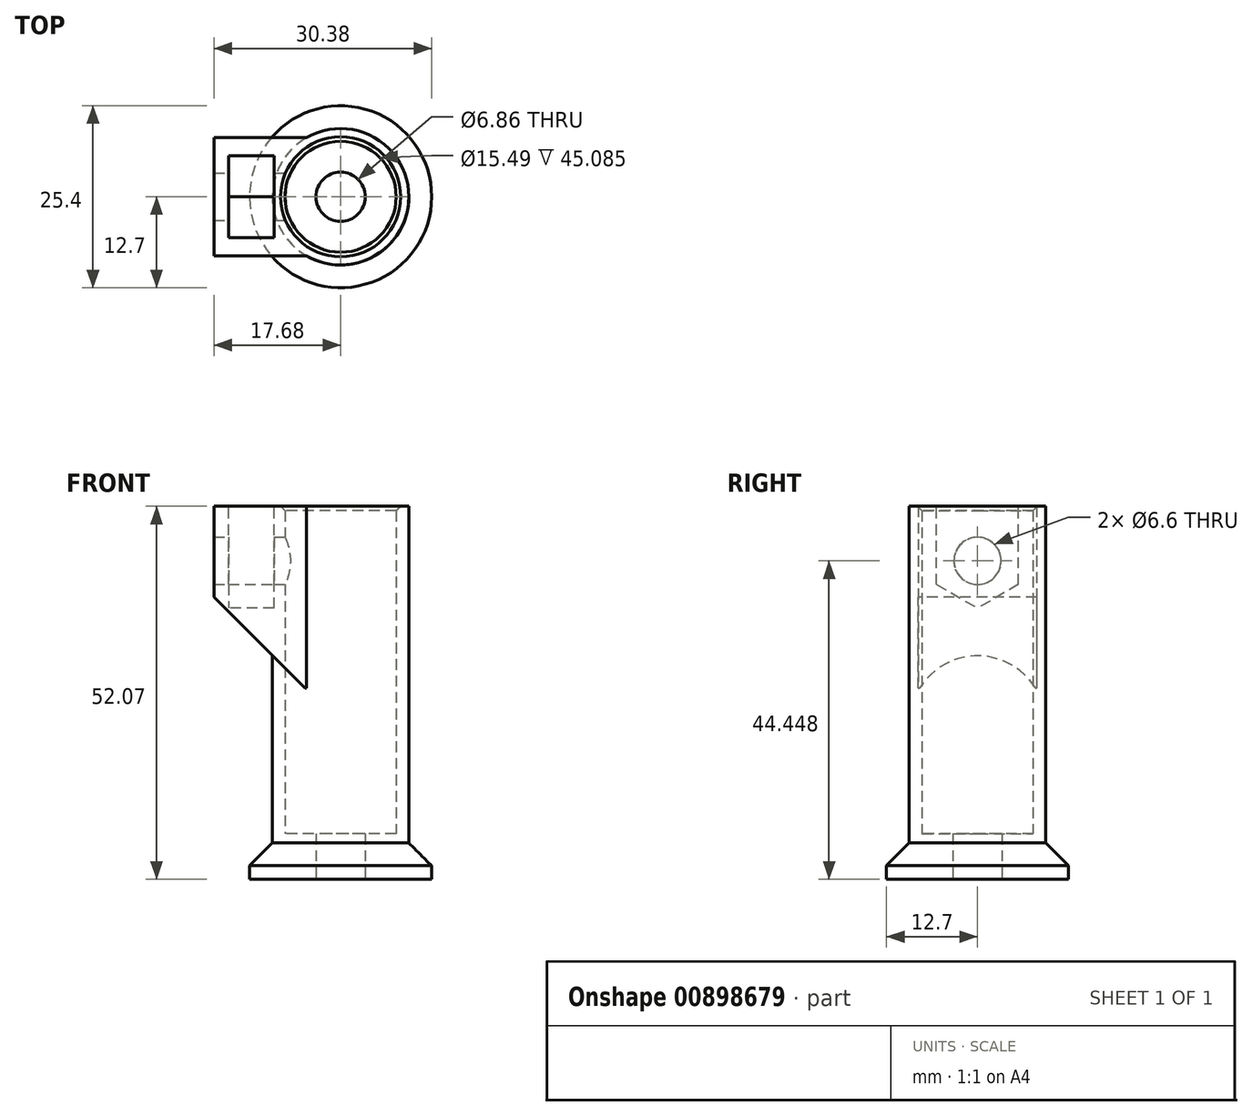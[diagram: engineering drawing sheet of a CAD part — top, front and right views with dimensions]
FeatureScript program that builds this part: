
annotation { "Feature Type Name" : "Feature", "Feature Type Description" : "" }
export const myFeature = defineFeature(function(context is Context, id is Id, definition is map)
    precondition{}
    {
        {
            var Q0;
            Q0=qCreatedBy(makeId("Top.planeOp"),FACE);
            var sketch = newSketch(context, id + "F0", { "sketchPlane" : qUnion([Q0])});
            skCircle(sketch, "E0", {"center": v(0, 0) * mm, "radius": 3.43 * mm});
            skCircle(sketch, "E1", {"center": v(0, 0) * mm, "radius": 12.7 * mm});
            skSolve(sketch);
        }
        {
            var Q0;
            Q0=makeQuery(id+"F0.imprint","IMPRINT",FACE,{"disambiguationData":[TD([[makeQuery(id+"F0.imprint","IMPRINT",EDGE,{"derivedFrom":sQuery(id+"F0.wireOp",EDGE,"E0")}),-1.0]])]});
            extrude(context, id + "F1", {"entities" : qUnion([Q0]), "depth" : 5.08 * mm, "offsetDistance" : 25.4 * mm});
        }
        {
            var Q0;
            Q0=makeQuery(id+"F1.opExtrude","CAP_EDGE",EDGE,{"disambiguationData":[OSD([sQuery(id+"F0.wireOp",EDGE,"E1")])],"isStart":false});
            chamfer(context, id + "F2", {"entities" : qUnion([Q0]), "width" : 3.17 * mm, "tangentPropagation" : true});
        }
        {
            var Q0;
            Q0=makeQuery(id+"F1.opExtrude","CAP_FACE",FACE,{"disambiguationData":[OSD([sQuery(id+"F0.wireOp",EDGE,"E0"),sQuery(id+"F0.wireOp",EDGE,"E1")])],"isStart":false});
            extrude(context, id + "F3", {"entities" : qUnion([Q0]), "operationType" : NewBodyOperationType.ADD, "depth" : 1.27 * mm, "offsetDistance" : 25.4 * mm});
        }
        {
            var Q0;
            Q0=makeQuery(id+"F3.opExtrude","CAP_FACE",FACE,{"disambiguationData":[OSD([sQuery(id+"F0.wireOp",EDGE,"E0"),sQuery(id+"F0.wireOp",EDGE,"E1")])],"isStart":false});
            var sketch = newSketch(context, id + "F4", { "sketchPlane" : qUnion([Q0])});
            skCircle(sketch, "E2", {"center": v(0, 0) * mm, "radius": 9.53 * mm});
            skCircle(sketch, "E3", {"center": v(0, 0) * mm, "radius": 7.75 * mm});
            skSolve(sketch);
        }
        {
            var Q0;
            Q0=makeQuery(id+"F4.imprint","IMPRINT",FACE,{"disambiguationData":[TD([[makeQuery(id+"F4.imprint","IMPRINT",EDGE,{"derivedFrom":sQuery(id+"F4.wireOp",EDGE,"E2")}),1.0]])]});
            extrude(context, id + "F5", {"entities" : qUnion([Q0]), "operationType" : NewBodyOperationType.ADD, "depth" : 20.32 * mm, "offsetDistance" : 25.4 * mm});
        }
        {
            var Q0;
            Q0=makeQuery(id+"F5.opExtrude","CAP_FACE",FACE,{"disambiguationData":[OSD([sQuery(id+"F4.wireOp",EDGE,"E2"),sQuery(id+"F4.wireOp",EDGE,"E3")])],"isStart":false});
            var sketch = newSketch(context, id + "F6", { "sketchPlane" : qUnion([Q0])});
            skLineSegment(sketch, "E4", {"start": v(0, 8.26) * mm, "end": v(-17.68, 8.25) * mm});
            skLineSegment(sketch, "E5", {"start": v(-17.68, 8.25) * mm, "end": v(-17.68, -8.26) * mm});
            skLineSegment(sketch, "E6", {"start": v(-17.68, -8.26) * mm, "end": v(0, -8.26) * mm});
            skArc(sketch, "E7", {"start": v(-4.75, -8.26) * mm, "mid": v(9.53, 0) * mm, "end": v(-4.75, 8.26) * mm});
            skCircle(sketch, "E8", {"center": v(0, 0) * mm, "radius": 8.26 * mm, "construction": true});
            skSolve(sketch);
        }
        {
            var Q0;
            {var subQ0=sQuery(id+"F6.wireOp",EDGE,"E7");Q0=makeQuery(id+"F6.imprint","IMPRINT",FACE,{"disambiguationData":[TD([[makeQuery(id+"F6.imprint","IMPRINT",EDGE,{"derivedFrom":subQ0}),1.0]])]});}
            var Q1;
            {var subQ0=sQuery(id+"F6.wireOp",EDGE,"E5");Q1=makeQuery(id+"F6.imprint","IMPRINT",FACE,{"disambiguationData":[TD([[makeQuery(id+"F6.imprint","IMPRINT",EDGE,{"derivedFrom":subQ0}),1.0]])]});}
            extrude(context, id + "F7", {"entities" : qUnion([Q0, Q1]), "operationType" : NewBodyOperationType.ADD, "depth" : 25.4 * mm, "offsetDistance" : 25.4 * mm});
        }
        {
            var Q0;
            Q0=makeQuery(id+"F7.opExtrude","CAP_EDGE",EDGE,{"disambiguationData":[OSD([sQuery(id+"F6.wireOp",EDGE,"E5")])],"isStart":true});
            chamfer(context, id + "F8", {"entities" : qUnion([Q0]), "width" : 12.7 * mm, "tangentPropagation" : true});
        }
        {
            var Q0;
            Q0=makeQuery(id+"F7.opExtrude","CAP_FACE",FACE,{"disambiguationData":[OSD([sQuery(id+"F4.wireOp",EDGE,"E3"),sQuery(id+"F6.wireOp",EDGE,"E4"),sQuery(id+"F6.wireOp",EDGE,"E5"),sQuery(id+"F6.wireOp",EDGE,"E6"),sQuery(id+"F6.wireOp",EDGE,"E7")])],"isStart":false});
            var sketch = newSketch(context, id + "F9", { "sketchPlane" : qUnion([Q0])});
            skLineSegment(sketch, "E9", {"start": v(0, 0) * mm, "end": v(-15.65, 0) * mm, "construction": true});
            skLineSegment(sketch, "E10.bottom", {"start": v(-15.65, 5.71) * mm, "end": v(-9.3, 5.71) * mm});
            skLineSegment(sketch, "E10.top", {"start": v(-15.65, -5.72) * mm, "end": v(-9.3, -5.72) * mm});
            skLineSegment(sketch, "E10.left", {"start": v(-15.65, 5.71) * mm, "end": v(-15.65, -5.72) * mm});
            skLineSegment(sketch, "E10.right", {"start": v(-9.3, 5.71) * mm, "end": v(-9.3, -5.71) * mm});
            skSolve(sketch);
        }
        {
            var Q0;
            Q0=qSketchRegion(id+"F9",true);
            extrude(context, id + "F10", {"entities" : qUnion([Q0]), "operationType" : NewBodyOperationType.REMOVE, "oppositeDirection" : true, "depth" : 14.22 * mm, "offsetDistance" : 25.4 * mm});
        }
        {
            var Q0;
            Q0=makeQuery(id+"F10.boolean.opBoolean","COPY",EDGE,{"derivedFrom":makeQuery(id+"F10.opExtrude","CAP_EDGE",EDGE,{"disambiguationData":[OSD([sQuery(id+"F9.wireOp",EDGE,"E10.bottom")])],"isStart":false})});
            var Q1;
            Q1=makeQuery(id+"F10.boolean.opBoolean","COPY",EDGE,{"derivedFrom":makeQuery(id+"F10.opExtrude","CAP_EDGE",EDGE,{"disambiguationData":[OSD([sQuery(id+"F9.wireOp",EDGE,"E10.top")])],"isStart":false})});
            chamfer(context, id + "F11", {"entities" : qUnion([Q0, Q1]), "chamferType" : ChamferType.OFFSET_ANGLE, "width" : 3.3 * mm, "oppositeDirection" : false, "angle" : 60 * degree, "tangentPropagation" : true});
        }
        {
            var Q0;
            Q0=makeQuery(id+"F10.boolean.opBoolean","COPY",FACE,{"derivedFrom":makeQuery(id+"F10.opExtrude","SWEPT_FACE",FACE,{"disambiguationData":[OSD([sQuery(id+"F9.wireOp",EDGE,"E10.left")])]})});
            var sketch = newSketch(context, id + "F12", { "sketchPlane" : qUnion([Q0])});
            skLineSegment(sketch, "E11", {"start": v(5.71, 41.15) * mm, "end": v(0, 37.85) * mm, "construction": true});
            skLineSegment(sketch, "E12", {"start": v(0, 37.85) * mm, "end": v(-5.72, 41.15) * mm, "construction": true});
            skLineSegment(sketch, "E13", {"start": v(-5.72, 41.15) * mm, "end": v(-5.72, 47.75) * mm, "construction": true});
            skLineSegment(sketch, "E14", {"start": v(-5.72, 47.75) * mm, "end": v(0, 51.05) * mm, "construction": true});
            skLineSegment(sketch, "E15", {"start": v(0, 51.05) * mm, "end": v(5.71, 47.75) * mm, "construction": true});
            skLineSegment(sketch, "E16", {"start": v(5.71, 47.75) * mm, "end": v(5.71, 41.15) * mm, "construction": true});
            skLineSegment(sketch, "E17", {"start": v(0, 37.85) * mm, "end": v(0, 44.45) * mm, "construction": true});
            skLineSegment(sketch, "E18", {"start": v(0, 44.45) * mm, "end": v(5.72, 41.15) * mm, "construction": true});
            skLineSegment(sketch, "E19", {"start": v(0, 44.45) * mm, "end": v(-5.72, 47.75) * mm, "construction": true});
            skLineSegment(sketch, "E20", {"start": v(0, 44.45) * mm, "end": v(0, 51.05) * mm, "construction": true});
            skCircle(sketch, "E21", {"center": v(0, 44.45) * mm, "radius": 3.3 * mm});
            skSolve(sketch);
        }
        {
            var Q0;
            Q0=qSketchRegion(id+"F12",true);
            extrude(context, id + "F13", {"entities" : qUnion([Q0]), "operationType" : NewBodyOperationType.REMOVE, "oppositeDirection" : true, "depth" : 25.4 * mm, "offsetDistance" : 25.4 * mm, "symmetric" : true});
        }
        {
            var Q0;
            Q0=makeQuery(id+"F7.opExtrude","CAP_EDGE",EDGE,{"disambiguationData":[OSD([sQuery(id+"F4.wireOp",EDGE,"E3")])],"isStart":false});
            chamfer(context, id + "F14", {"entities" : qUnion([Q0]), "width" : 0.64 * mm, "tangentPropagation" : true});
        }
    });
